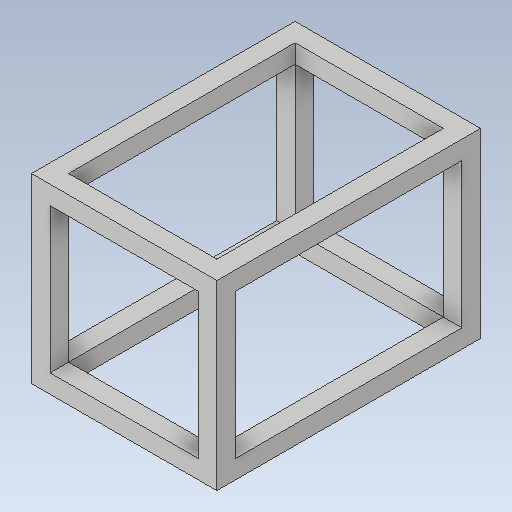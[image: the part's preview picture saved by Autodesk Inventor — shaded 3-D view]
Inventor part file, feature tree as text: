
AUTODESK INVENTOR PART (.ipt)
format: ipt  version: 2020 (Build 240168000, 168)  size: 145,920 bytes
history: native  units: in
note: dims shown in document units (in); Inventor stores cm internally (conversion verified against a paired STEP export)
features: extrude x4, sketch x4
ambient origin geometry x8: Origin, YZ Plane, XZ Plane, XY Plane, X Axis, Y Axis, Z Axis, Center Point
bodies: Solid1 (feature_tree)
feature tree (8):
  extrude  "Extrusion1"  Depth=7.7272in
  extrude  "Extrusion2"  Depth=0.7874in
  extrude  "Extrusion3"  Depth=0.7874in
  extrude  "Extrusion4"  Depth=0.7874in TaperAngle=0.0deg
  sketch  "Sketch1"  dims[d0=7.874in d1=7.7272in]
  sketch  "Sketch2"  dims[d2=11.1929in d3=0.0in d4=0.7874in]
  sketch  "Sketch3"  dims[d5=0.7874in d6=0.7874in]
  sketch  "Sketch4"  dims[d7=0.7874in d8=35.4331in d9=0.0in d10=0.7874in d11=0.7874in d12=0.7874in d13=0.7874in d14=35.4331in d15=0.0in d16=35.4331in d17=0.0in]
